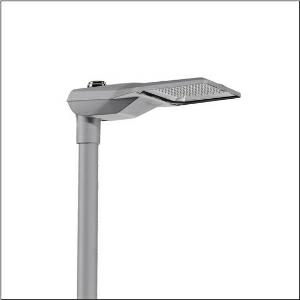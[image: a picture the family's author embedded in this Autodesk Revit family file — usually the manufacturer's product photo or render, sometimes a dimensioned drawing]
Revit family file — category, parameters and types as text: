
# Revit family: streetlight_sl_21_midi___st0_5a_5xe7b47n08lb_dab4
name_source: partatom
category: Lighting Fixtures
units: mm (PartAtom-declared; Revit-internal decimal feet)

## family parameters
Cut with Voids When Loaded = No
Host = Face
Light Source = No
Part Type = Normal
Room Calculation Point = No
Round Connector Dimension = Use Diameter
Shared = No

## types (1)
- --- (1 x LED, 14950 lm, 98.3 W, 4000K)
    Apparent Load = 98 VA
    CIE Flux Codes = 41 75 97 100 100
    Color Rendering = 70
    Color Temperature = 4000K
    Default Elevation = 1800 mm
    Description = Streetlight SL 21 midi, mast luminaire, primary light control with lens, of PMMA, primary optical cover: cover, of toughened safety glass, transparent, light distribution: ST0.5a, light emission: direct distribution, primary light characteristic: asymmetric, installation type: side-entry, LED, 3G 2.5mm², High Power LED, rated luminous flux: 14.950lm, luminous efficacy: 152lm/W, light colour: 740, colour temperature: 4000K, control gear: NEMA (7pin), control: overheat protection, pre-setting: linear dimming characteristic, constant luminous flux control, time-dependent luminous flux control, flexible luminous flux parameterisation, mains connection: 220..240V, AC, 50/60Hz, connection cable pre-assembled, cable length: 10,5m, wiring characteristics: H05VV-F, start of lifetime: 98W, end of service life: 101W, reduction: 45W, luminaire housing, of diecast aluminium (EN AC-44300), powder-coated, Siteco® metallic grey (DB 702S), corrosivity category C5 mid according to DIN EN ISO 12944, multi-level sealing system, sealing non-destructively replaceable, inclination adjustable: 0°, 5°, 10°, 15°, length: 644mm, width: 335mm, height: 110mm, spigot size: 42mm (side-entry), mounting height: 4..8m, protection rating (complete): IP66, insulation class (complete): insulation class I (protective earthing), certification: CE, ENEC, ENEC+, VDE, impact resistance: IK10, permissible operating ambient temperature for outdoor applications: -40..+50°C, standard-compliant lighting for roads and squares, packaging unit: 1 piece

Light Distribution: ST0.5a
    Height = 111 mm
    Lamp = 1 x LED
    Lamp Light Flux = 14950 lm
    Lamp Power = 98.3 W
    Lamp count = 1
    Length = 644 mm
    Luminous efficacy = 152 lm/W
    Manufacturer = Siteco
    ModVariant = No
    Model = 5XE7B47N08LB
    Number of Poles = 1
    OnlyDefault = Yes
    Power Factor = 1
    Product Name = Streetlight SL 21 midi | ST0.5a
    Product group = mast luminaire | pylon top
    ProductGroupID = 6100
    Protection Class = Protection class I
    Protection Degree = IP 66
    RLX_Detail_Level = 1
    RLX_Emergency_Light_Flux = 0 lm
    RLX_Emergency_Type = 0
    RLX_Emergency_Type_DB = No
    RlxData = <blob elided: 37693 chars, md5=676db756>
    Socket = socket
    Standby Power = 0 W
    System Light Flux = 14950 lm
    System Power = 98 W
    Type Comments = factory setting: luminous flux: 100 % | dim-lin: 254 | 1020 mA
    Type Image = l_1294377.jpg
    URL = http://relux.com
    VarID = @adj_158779
    Voltage = 0 V
    Weight = 0.00 kg
    Width = 336 mm

## geometry (parser evidence)
native form markers: Blend x4, Sweep x12
no freeform markers — native parametric forms only
